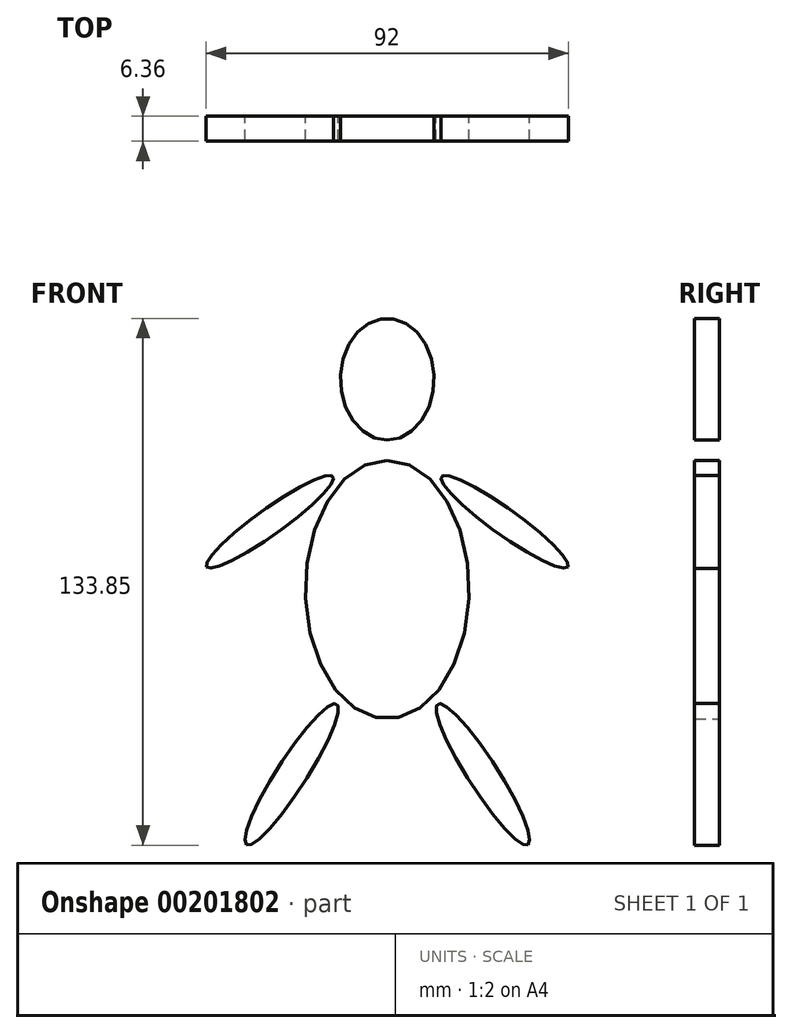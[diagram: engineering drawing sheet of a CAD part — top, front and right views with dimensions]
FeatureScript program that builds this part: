
annotation { "Feature Type Name" : "Feature", "Feature Type Description" : "" }
export const myFeature = defineFeature(function(context is Context, id is Id, definition is map)
    precondition{}
    {
        {
            var Q0;
            Q0=qCreatedBy(makeId("Front.planeOp"),FACE);
            var sketch = newSketch(context, id + "F0", { "sketchPlane" : qUnion([Q0])});
            skEllipse(sketch, "E0", {"center": v(0, 53.44) * mm, "majorRadius": 15.45 * mm, "minorRadius": 11.91 * mm, "majorAxis": v(0, -1)});
            skSolve(sketch);
        }
        {
            var Q0;
            Q0 = qSketchRegion(id + "F0", true);
            extrude(context, id + "F1", {"entities" : qUnion([Q0]), "endBound" : BoundingType.SYMMETRIC, "depth" : 6.35 * mm});
        }
        {
            var Q0;
            Q0=qCreatedBy(makeId("Front.planeOp"),FACE);
            var sketch = newSketch(context, id + "F2", { "sketchPlane" : qUnion([Q0])});
            skEllipse(sketch, "E1", {"center": v(0, 0) * mm, "majorRadius": 32.84 * mm, "minorRadius": 20.8 * mm, "majorAxis": v(0, 1)});
            skSolve(sketch);
        }
        {
            var Q0;
            Q0=makeQuery(id+"F2.imprint","IMPRINT",FACE,{"disambiguationData":[TD([[makeQuery(id+"F2.imprint","IMPRINT",EDGE,{"derivedFrom":sQuery(id+"F2.wireOp",EDGE,"E1")}),1.0]])]});
            extrude(context, id + "F3", {"entities" : qUnion([Q0]), "endBound" : BoundingType.SYMMETRIC, "depth" : 6.35 * mm});
        }
        {
            var Q0;
            Q0=qCreatedBy(makeId("Front.planeOp"),FACE);
            var sketch = newSketch(context, id + "F4", { "sketchPlane" : qUnion([Q0])});
            skEllipse(sketch, "E2", {"center": v(29.83, 17.2) * mm, "majorRadius": 19.74 * mm, "minorRadius": 3.33 * mm, "majorAxis": v(0.81, -0.58)});
            skPoint(sketch, "E3.centerSnap0", {"position": v(45.89, 5.74) * mm});
            skSolve(sketch);
        }
        {
            var Q0;
            Q0=makeQuery(id+"F4.imprint","IMPRINT",FACE,{"disambiguationData":[TD([[makeQuery(id+"F4.imprint","IMPRINT",EDGE,{"derivedFrom":sQuery(id+"F4.wireOp",EDGE,"E2")}),1.0]])]});
            extrude(context, id + "F5", {"entities" : qUnion([Q0]), "endBound" : BoundingType.SYMMETRIC, "depth" : 6.35 * mm});
        }
        {
            var Q0;
            Q0=qCreatedBy(makeId("Front.planeOp"),FACE);
            var sketch = newSketch(context, id + "F6", { "sketchPlane" : qUnion([Q0])});
            skEllipse(sketch, "E4", {"center": v(24.31, -46.97) * mm, "majorRadius": 21.21 * mm, "minorRadius": 3.8 * mm, "majorAxis": v(0.54, -0.84)});
            skSolve(sketch);
        }
        {
            var Q0;
            Q0=makeQuery(id+"F6.imprint","IMPRINT",FACE,{"disambiguationData":[TD([[makeQuery(id+"F6.imprint","IMPRINT",EDGE,{"derivedFrom":sQuery(id+"F6.wireOp",EDGE,"E4")}),1.0]])]});
            extrude(context, id + "F7", {"entities" : qUnion([Q0]), "endBound" : BoundingType.SYMMETRIC, "depth" : 6.35 * mm});
        }
        {
            var Q0;
            Q0=makeQuery(id+"F5.opExtrude","SWEPT_BODY",BODY,{"disambiguationData":[OSD([sQuery(id+"F4.wireOp",EDGE,"E2")])]});
            var Q1;
            Q1=makeQuery(id+"F7.opExtrude","SWEPT_BODY",BODY,{"disambiguationData":[OSD([sQuery(id+"F6.wireOp",EDGE,"E4")])]});
            var Q2;
            Q2=qCreatedBy(makeId("Right.planeOp"),FACE);
            mirror(context, id + "F8", {"entities" : qUnion([Q0, Q1]), "mirrorPlane" : qUnion([Q2])});
        }
    });
